# Revit family: Legrand_Coffrets HYPRA équipés monoprise IP44 avec disjoncteur
name_source: partatom
category: Equipement électrique
units: mm (PartAtom-declared; Revit-internal decimal feet)

## family parameters
Basée sur le plan de construction = Non
Configuration du panneau = Deux colonnes, circuits au sein
Cote de connecteur circulaire = Utiliser le diamètre
Couper avec des vides une fois chargée = Non
Numéro OmniClass = 23.80.30.11.17
Partagée = Non
Point de calcul de pièce = Non
Titre OmniClass = Distribution Boards and Control Panels
Toujours verticalement = Oui
Type d'élément = Tableau de raccordement

## types (8) — shared parameters
Classe de protection = IP44
Conditions Générale d'Utilisation = https://export.legrand.com
Description = Coffrets Hypra équipé
Fabricant = Legrand
Protection = disjoncteur
URL = www.legrand.fr
zero-valued in all types: Elévation par défaut

## per-type parameters (varying)
| type | Coffret équipé | IEC 61439-2 | IEC 61439-3 | Référence 059206 | Référence 059213 | Référence 059218 | Référence 059239 | Référence 059240 | Référence 059246 | Référence 059253 | Référence 059258 | Tension |
| Référence 059206 | 2P+T | 16A | 16A | Oui | Non | Non | Non | Non | Oui | Non | Non | 200 à 250 V |
| Référence 059246 | 2P+T | 32A | 32A | Oui | Non | Non | Non | Non | Oui | Non | Non | 200 à 250 V |
| Référence 059213 | 3P+T | 16A | 16A | Non | Oui | Oui | Non | Non | Non | Non | Non | 380 à 415 V |
| Référence 059218 | 3P+N+T | 16A | 16A | Non | Oui | Oui | Non | Non | Non | Non | Non | 380 à 415 V |
| Référence 059253 | 3P+T | 32A | 32A | Non | Non | Non | Non | Non | Non | Oui | Oui | 380 à 415 V |
| Référence 059258 | 3P+N+T | 32A | 32A | Non | Non | Non | Non | Non | Non | Oui | Oui | 380 à 415 V |
| Référence 059239 | 3P+T | 50A |  | Non | Non | Non | Oui | Oui | Non | Non | Non | 380 à 415 V |
| Référence 059240 | 3P+N+T | 50A |  | Non | Non | Non | Oui | Oui | Non | Non | Non | 380 à 415 V |

note: column(s) folded — value = type name in every type: Modèle
